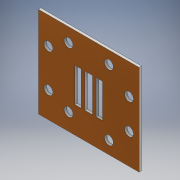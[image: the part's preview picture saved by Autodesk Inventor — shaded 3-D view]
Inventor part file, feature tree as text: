
AUTODESK INVENTOR PART (.ipt)
format: ipt  version: 2017 (Build 210142000, 142)  size: 168,960 bytes
history: native  units: mm
features: extrude x1, sketch x1
ambient origin geometry x8: Origin, YZ Plane, XZ Plane, XY Plane, X Axis, Y Axis, Z Axis, Center Point
bodies: Body1 (feature_tree)
feature tree (2):
  extrude  "Extrusion3"  Depth=40.0mm
  sketch  "Sketch1"  dims[d0=36.0mm d1=40.0mm d4=3.5mm d5=6.0mm d7=3.5mm d8=3.5mm d14=32.0mm d15=4.0mm d16=4.0mm d17=4.0mm d19=3.5mm d20=3.5mm d21=3.5mm d23=5.0mm d24=5.0mm d28=16.0mm d29=12.0mm d30=3.5mm d31=16.0mm d32=10.705065mm d33=25.75mm d34=5.496796mm d35=29.25mm d42=3.0mm d45=1.5mm d53=2.5mm d54=90.0deg d56=23.0mm d61=12.0mm d62=12.0mm d66=13.5mm d67=2.5mm d68=1.0mm d69=0.0mm d70=14.5mm d71=4.952167mm d72=24.0mm d73=13.5mm d74=4.952167mm d75=0.0mm d76=13.5mm d77=17.0mm d78=18.5mm d79=21.5mm d80=23.0mm d81=12.0mm]
